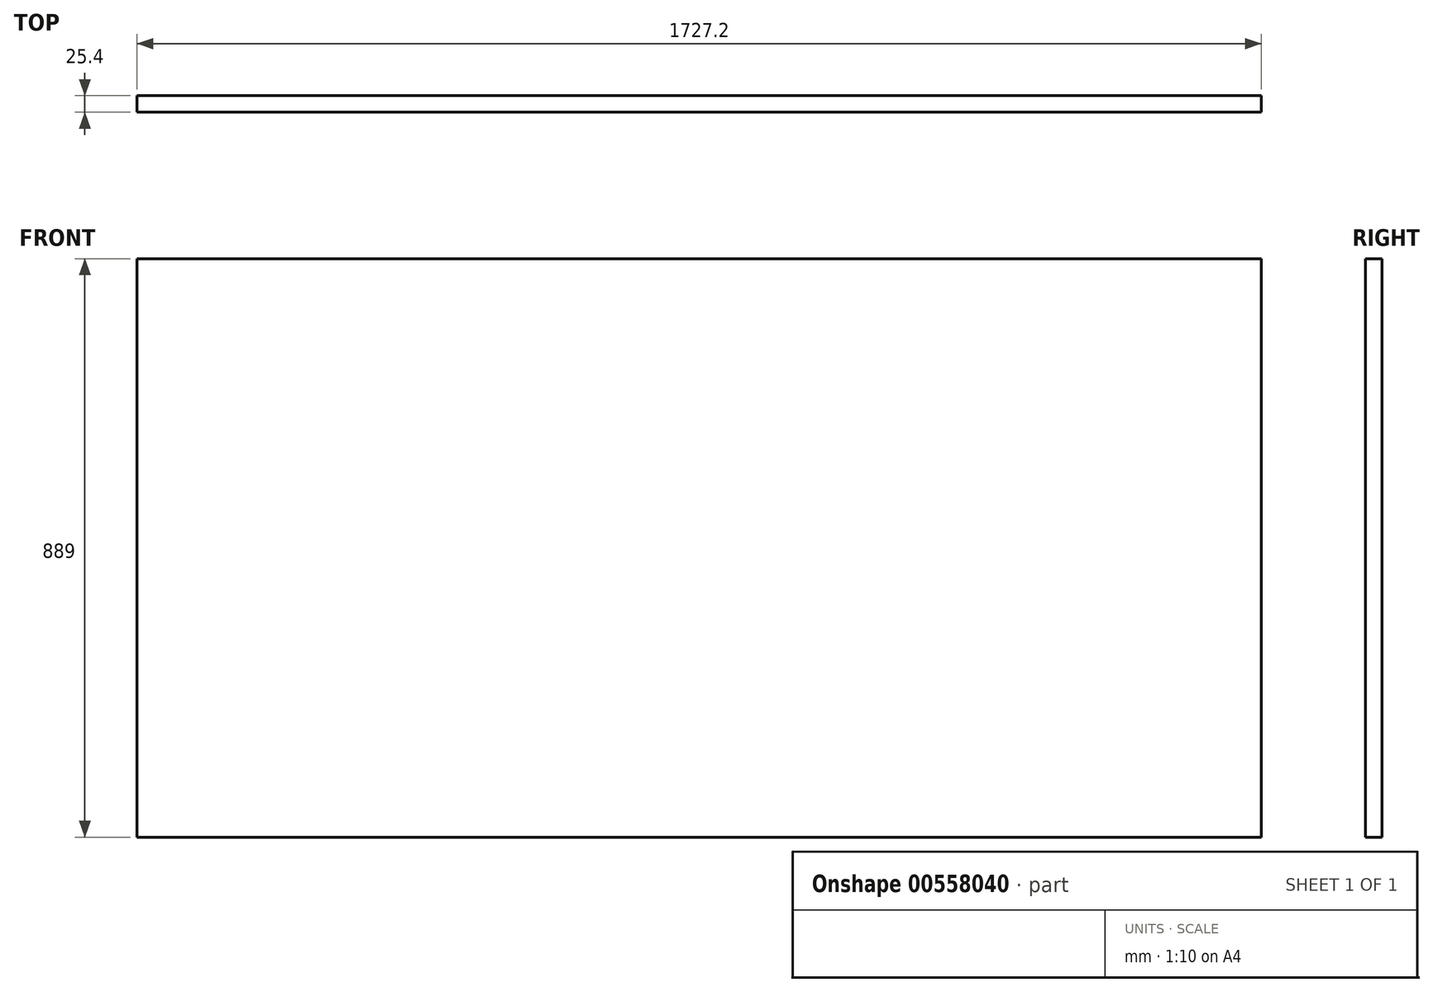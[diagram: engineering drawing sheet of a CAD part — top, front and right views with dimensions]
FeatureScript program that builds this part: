
annotation { "Feature Type Name" : "Feature", "Feature Type Description" : "" }
export const myFeature = defineFeature(function(context is Context, id is Id, definition is map)
    precondition{}
    {
        {
            var Q0;
            Q0=qCreatedBy(makeId("Front.planeOp"),FACE);
            var sketch = newSketch(context, id + "F0", { "sketchPlane" : qUnion([Q0])});
            skLineSegment(sketch, "E0.bottom", {"start": v(-858.05, 666.85) * mm, "end": v(869.15, 666.85) * mm});
            skLineSegment(sketch, "E0.top", {"start": v(-858.05, -222.15) * mm, "end": v(869.15, -222.15) * mm});
            skLineSegment(sketch, "E0.left", {"start": v(-858.05, 666.85) * mm, "end": v(-858.05, -222.15) * mm});
            skLineSegment(sketch, "E0.right", {"start": v(869.15, 666.85) * mm, "end": v(869.15, -222.15) * mm});
            skSolve(sketch);
        }
        {
            var Q0;
            Q0=makeQuery(id+"F0.imprint","IMPRINT",FACE,{"disambiguationData":[TD([[makeQuery(id+"F0.imprint","IMPRINT",EDGE,{"derivedFrom":sQuery(id+"F0.wireOp",EDGE,"E0.bottom")}),-1.0]])]});
            extrude(context, id + "F1", {"entities" : qUnion([Q0]), "depth" : 25.4 * mm, "offsetDistance" : 25.4 * mm});
        }
    });
